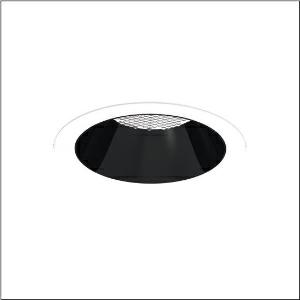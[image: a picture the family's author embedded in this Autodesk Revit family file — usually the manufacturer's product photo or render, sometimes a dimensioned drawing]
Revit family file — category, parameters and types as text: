
# Revit family: lunis_21_xl_51db17tf91c
name_source: partatom
category: Lighting Fixtures
units: mm (PartAtom-declared; Revit-internal decimal feet)

## family parameters
Cut with Voids When Loaded = No
Host = Face
Light Source = No
Part Type = Normal
Room Calculation Point = No
Round Connector Dimension = Use Diameter
Shared = No

## types (1)
- --- (1 x LED, 3510 lm, 25.4 W, 4000K)
    Apparent Load = 25 VA
    CIE Flux Codes = 95 98 100 100 100
    Color Rendering = 80
    Color Temperature = 4000K
    Default Elevation = 1800 mm
    Description = Lunis 21,  XL, downlight, light control with lens, of PMMA, anti glare with reflector, of aluminium, light emission: direct distribution, LED rated luminous flux: 2.060lm, light colour: 8tw, with terminal, 5-pole, mains connection: 220..240V, AC/DC, 0/50..60Hz, housing, round, of diecast aluminium, traffic white (RAL 9016), diameter: 230mm, clamping range: 1..40mm, protection rating (complete): IP20, protection rating (on room side): IP54, insulation class (complete): insulation class II (safety insulation), certification: CE, impact resistance: IK03, packaging unit: 1 piece
    Height = 0 mm  [stored 0 ft]
    Lamp = 1 x LED
    Lamp Light Flux = 3510 lm
    Lamp Power = 25.4 W
    Lamp count = 1
    Length = 230 mm
    Luminous efficacy = 138 lm/W
    Manufacturer = Siteco
    ModVariant = No
    Model = 51DB17TF91C
    Mounting Place = Ceiling
    Mounting Type = Recessed
    Number of Poles = 1
    OnlyDefault = Yes
    Power Factor = 1
    Product Name = Lunis 21 XL
    Product group = downlight
    ProductGroupID = 400
    Protection Class = Protection class II
    Protection Degree = IP 20
    RLX_Detail_Level = 1
    RLX_Emergency_Light_Flux = 0 lm
    RLX_Emergency_Type = 0
    RLX_Emergency_Type_DB = No
    RlxData = <blob elided: 19257 chars, md5=dc9352c8>
    Socket = socket
    Standby Power = 0 W
    System Light Flux = 3510 lm
    System Power = 25 W
    Type Comments = individual setting: colour temperature 4000K, luminous flux: 100 % | (ON | ON | OFF | OFF) | 700 mA
    Type Image = l_1291161.jpg
    URL = http://relux.com
    VarID = @adj_018947
    Voltage = 0 V
    Weight = 0.00 kg
    Width = 0 mm  [stored 0 ft]

note: [stored X ft] marks values corroborated as IEEE doubles in the binary element streams (Revit-internal decimal feet)

## geometry (parser evidence)
native form markers: Blend x4, Sweep x10
no freeform markers — native parametric forms only
